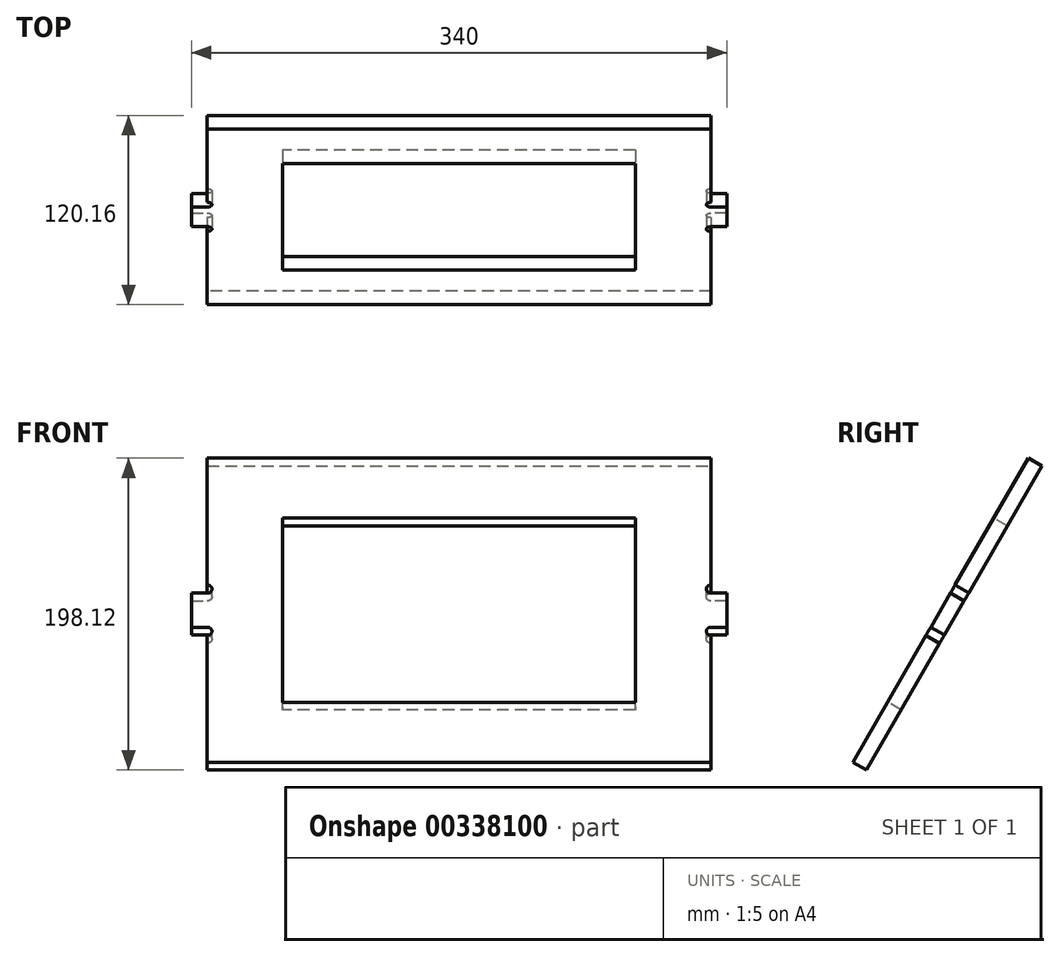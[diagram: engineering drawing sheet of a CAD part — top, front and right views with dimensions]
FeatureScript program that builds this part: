
annotation { "Feature Type Name" : "Feature", "Feature Type Description" : "" }
export const myFeature = defineFeature(function(context is Context, id is Id, definition is map)
    precondition{}
    {
        {
            var Q0;
            Q0=qCreatedBy(makeId("Front.planeOp"),FACE);
            var sketch = newSketch(context, id + "F0", { "sketchPlane" : qUnion([Q0])});
            skLineSegment(sketch, "E0", {"start": v(0, 0) * mm, "end": v(75.07, 0) * mm});
            skSolve(sketch);
        }
        {
            var Q0;
            Q0=sQuery(id+"F0.wireOp",EDGE,"E0");
            cPlane(context, id + "F1", {"entities" : qUnion([Q0]), "cplaneType" : CPlaneType.LINE_ANGLE, "offset" : 25 * mm, "angle" : 330 * degree, "width" : 150 * mm, "height" : 150 * mm});
        }
        {
            var Q0;
            Q0=qCreatedBy(id+"F1.planeOp",FACE);
            var sketch = newSketch(context, id + "F2", { "sketchPlane" : qUnion([Q0])});
            skLineSegment(sketch, "E1.bottom", {"start": v(-224, 144.75) * mm, "end": v(0, 144.75) * mm});
            skLineSegment(sketch, "E1.top", {"start": v(-224, 9.75) * mm, "end": v(0, 9.75) * mm});
            skLineSegment(sketch, "E1.left", {"start": v(-224, 144.75) * mm, "end": v(-224, 9.75) * mm});
            skLineSegment(sketch, "E1.right", {"start": v(0, 144.75) * mm, "end": v(0, 9.75) * mm});
            skLineSegment(sketch, "E2.0", {"start": v(-272, 188.75) * mm, "end": v(-112, 188.75) * mm});
            skLineSegment(sketch, "E3.0", {"start": v(-272, 188.75) * mm, "end": v(-272, 95.75) * mm});
            skLineSegment(sketch, "E4", {"start": v(-112, 300.93) * mm, "end": v(-112, -139.45) * mm, "construction": true});
            skLineSegment(sketch, "E5", {"start": v(-272, -34.25) * mm, "end": v(-112, -34.25) * mm});
            skLineSegment(sketch, "E6.MirrorCS", {"start": v(48, 188.75) * mm, "end": v(-112, 188.75) * mm});
            skLineSegment(sketch, "E7.MirrorCS", {"start": v(48, -34.25) * mm, "end": v(-112, -34.25) * mm});
            skLineSegment(sketch, "E8.MirrorCS", {"start": v(48, 188.75) * mm, "end": v(48, 95.75) * mm});
            skLineSegment(sketch, "E9", {"start": v(48, 77.25) * mm, "end": v(-112, 77.25) * mm, "construction": true});
            skLineSegment(sketch, "E10.bottom", {"start": v(58, 89.75) * mm, "end": v(48, 89.75) * mm});
            skLineSegment(sketch, "E10.top", {"start": v(58, 64.75) * mm, "end": v(48, 64.75) * mm});
            skLineSegment(sketch, "E10.left", {"start": v(58, 89.75) * mm, "end": v(58, 64.75) * mm});
            skPoint(sketch, "E10.middle", {"position": v(48, 77.25) * mm});
            skPoint(sketch, "E11.orphan", {"position": v(38, 64.75) * mm});
            skLineSegment(sketch, "E12.trimOffspring", {"start": v(48, 95.75) * mm, "end": v(48, 188.75) * mm, "construction": true});
            skLineSegment(sketch, "E13.trimOffspring", {"start": v(48, 64.75) * mm, "end": v(48, 61.75) * mm});
            skLineSegment(sketch, "E14.MirrorCS", {"start": v(-282, 64.75) * mm, "end": v(-272, 64.75) * mm});
            skLineSegment(sketch, "E15.MirrorCS", {"start": v(-282, 89.75) * mm, "end": v(-272, 89.75) * mm});
            skLineSegment(sketch, "E16.MirrorCS", {"start": v(-282, 89.75) * mm, "end": v(-282, 64.75) * mm});
            skArc(sketch, "E17", {"start": v(48, 95.75) * mm, "mid": v(45, 92.75) * mm, "end": v(48, 89.75) * mm});
            skArc(sketch, "E18", {"start": v(48, 64.75) * mm, "mid": v(45, 61.75) * mm, "end": v(48, 58.75) * mm});
            skLineSegment(sketch, "E19.trimOffspring", {"start": v(48, 58.75) * mm, "end": v(48, -34.25) * mm});
            skArc(sketch, "E20.MirrorCS", {"start": v(-272, 64.75) * mm, "mid": v(-269, 61.75) * mm, "end": v(-272, 58.75) * mm});
            skArc(sketch, "E21.MirrorCS", {"start": v(-272, 95.75) * mm, "mid": v(-269, 92.75) * mm, "end": v(-272, 89.75) * mm});
            skLineSegment(sketch, "E22.trimOffspring", {"start": v(-272, 58.75) * mm, "end": v(-272, -34.25) * mm});
            skPoint(sketch, "E23.MirrorCS.end.orphan", {"position": v(-272, 188.75) * mm});
            skLineSegment(sketch, "E24", {"start": v(48, 188.75) * mm, "end": v(48, 188.75) * mm});
            skLineSegment(sketch, "E25", {"start": v(-272, -34.25) * mm, "end": v(-272, -34.25) * mm});
            skSolve(sketch);
        }
        {
            var Q0;
            Q0=makeQuery(id+"F2.imprint","IMPRINT",FACE,{"disambiguationData":[TD([[makeQuery(id+"F2.imprint","IMPRINT",EDGE,{"derivedFrom":sQuery(id+"F2.wireOp",EDGE,"E1.bottom")}),1.0]])]});
            extrude(context, id + "F3", {"entities" : qUnion([Q0]), "depth" : 10 * mm});
        }
    });
